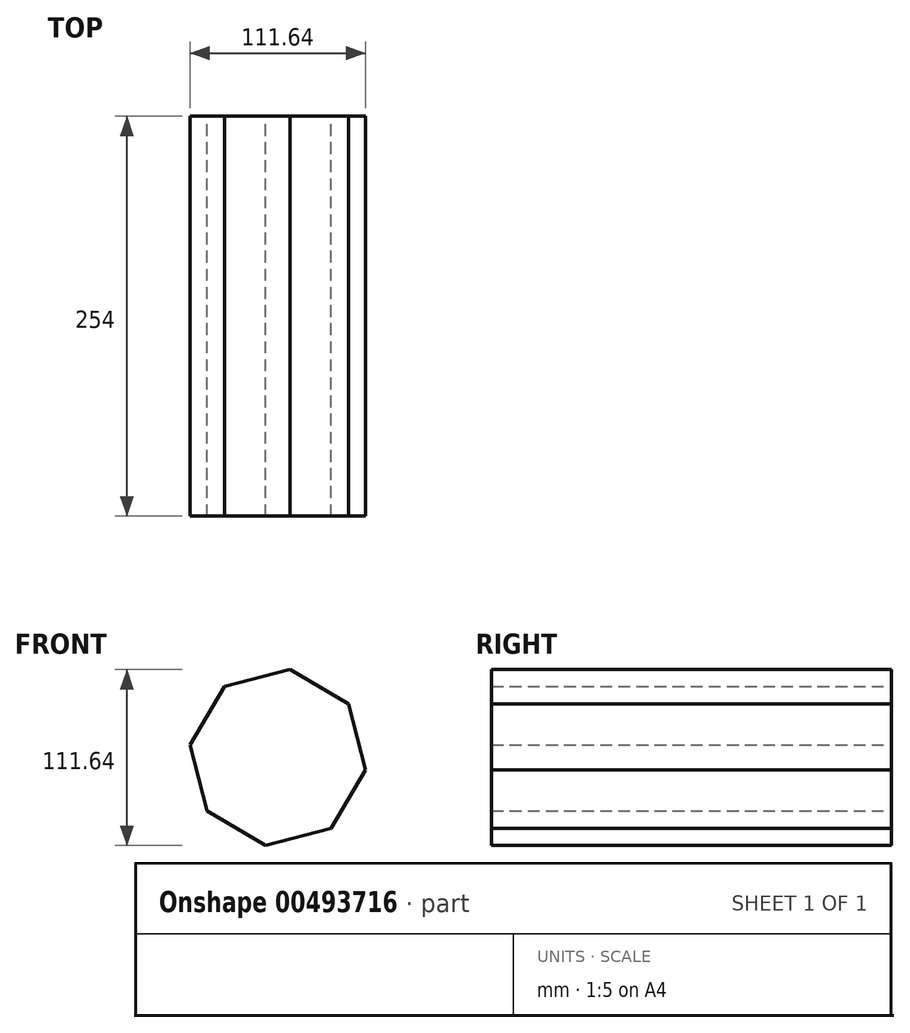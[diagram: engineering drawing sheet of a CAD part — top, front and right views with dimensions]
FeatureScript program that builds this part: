
annotation { "Feature Type Name" : "Feature", "Feature Type Description" : "" }
export const myFeature = defineFeature(function(context is Context, id is Id, definition is map)
    precondition{}
    {
        {
            var Q0;
            Q0=qCreatedBy(makeId("Front.planeOp"),FACE);
            var sketch = newSketch(context, id + "F0", { "sketchPlane" : qUnion([Q0])});
            skCircle(sketch, "E0.cCircle", {"center": v(0, 0) * mm, "radius": 56.37 * mm, "construction": true});
            skLineSegment(sketch, "E0.0", {"start": v(7.87, 55.82) * mm, "end": v(45.03, 33.9) * mm});
            skLineSegment(sketch, "E0.1", {"start": v(45.03, 33.9) * mm, "end": v(55.82, -7.87) * mm});
            skLineSegment(sketch, "E0.2", {"start": v(55.82, -7.87) * mm, "end": v(33.9, -45.03) * mm});
            skLineSegment(sketch, "E0.3", {"start": v(33.9, -45.03) * mm, "end": v(-7.87, -55.82) * mm});
            skLineSegment(sketch, "E0.4", {"start": v(-7.87, -55.82) * mm, "end": v(-45.03, -33.9) * mm});
            skLineSegment(sketch, "E0.5", {"start": v(-45.03, -33.9) * mm, "end": v(-55.82, 7.87) * mm});
            skLineSegment(sketch, "E0.6", {"start": v(-55.82, 7.87) * mm, "end": v(-33.9, 45.03) * mm});
            skLineSegment(sketch, "E0.7", {"start": v(-33.9, 45.03) * mm, "end": v(7.87, 55.82) * mm});
            skSolve(sketch);
        }
        {
            var Q0;
            Q0 = qSketchRegion(id + "F0", true);
            extrude(context, id + "F1", {"entities" : qUnion([Q0]), "depth" : 254 * mm});
        }
    });
